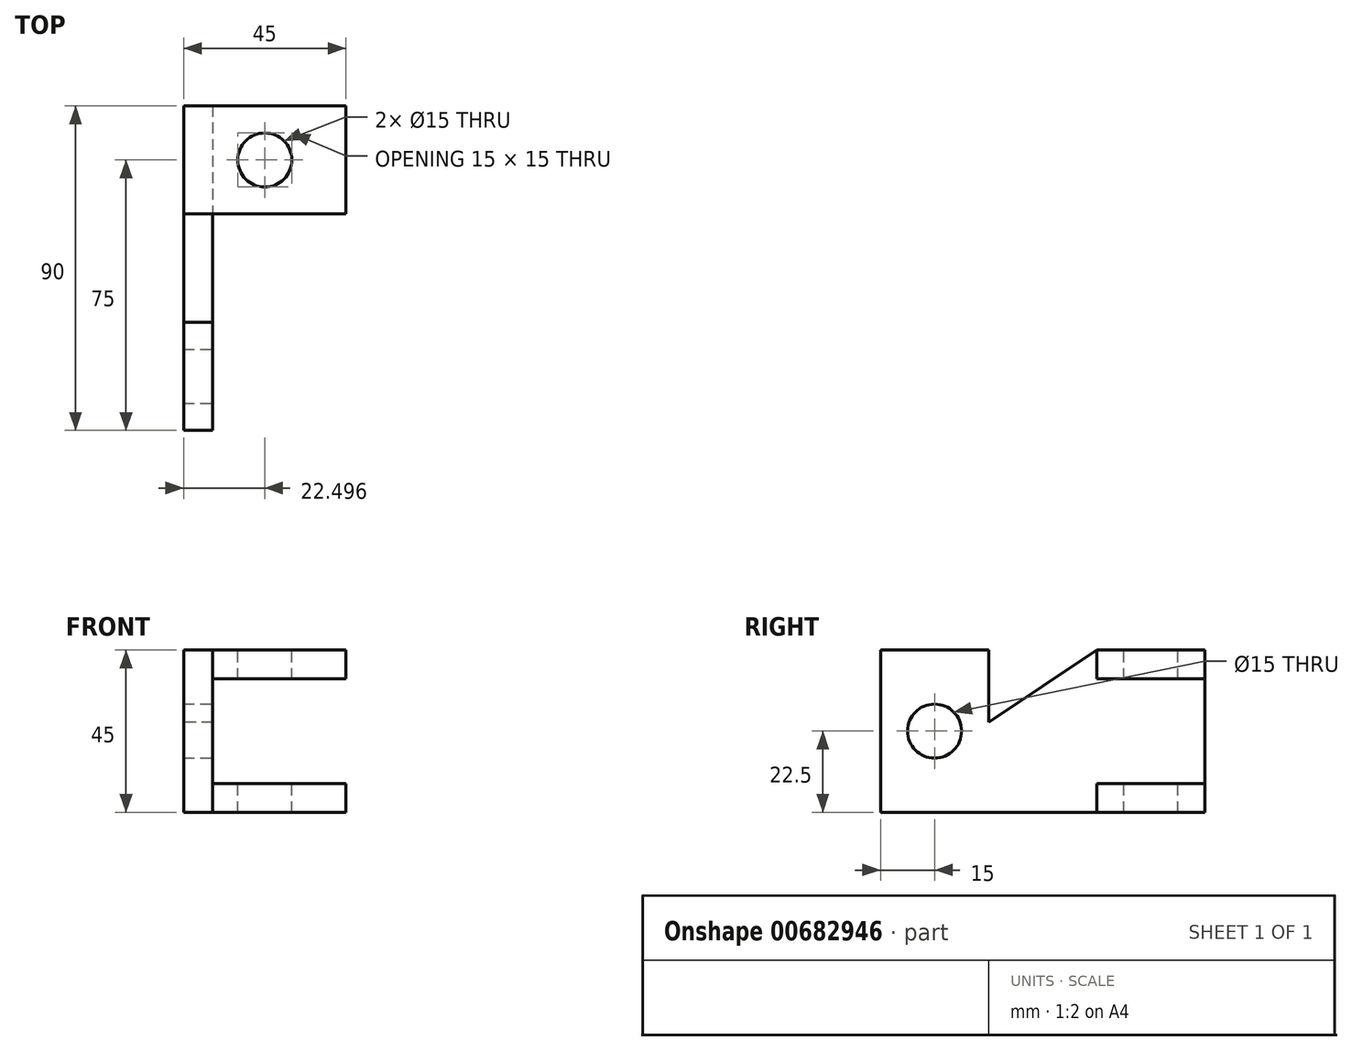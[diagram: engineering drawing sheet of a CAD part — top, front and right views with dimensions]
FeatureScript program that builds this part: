
annotation { "Feature Type Name" : "Feature", "Feature Type Description" : "" }
export const myFeature = defineFeature(function(context is Context, id is Id, definition is map)
    precondition{}
    {
        {
            var Q0;
            Q0=qCreatedBy(makeId("Right.planeOp"),FACE);
            var sketch = newSketch(context, id + "F0", { "sketchPlane" : qUnion([Q0])});
            skLineSegment(sketch, "E0", {"start": v(0, 45) * mm, "end": v(0, 0) * mm});
            skLineSegment(sketch, "E1", {"start": v(0, 0) * mm, "end": v(90, 0) * mm});
            skLineSegment(sketch, "E2", {"start": v(90, 0) * mm, "end": v(90, 45) * mm});
            skLineSegment(sketch, "E3", {"start": v(90, 45) * mm, "end": v(60, 45) * mm});
            skLineSegment(sketch, "E4", {"start": v(60, 45) * mm, "end": v(30, 25) * mm});
            skLineSegment(sketch, "E5", {"start": v(30, 25) * mm, "end": v(30, 45) * mm});
            skLineSegment(sketch, "E6", {"start": v(30, 45) * mm, "end": v(0, 45) * mm});
            skSolve(sketch);
        }
        {
            var Q0;
            Q0 = qSketchRegion(id + "F0", true);
            extrude(context, id + "F1", {"entities" : qUnion([Q0]), "depth" : 8 * mm, "offsetDistance" : 25.4 * mm});
        }
        {
            var Q0;
            Q0=makeQuery(id+"F1.opExtrude","CAP_FACE",FACE,{"disambiguationData":[OSD([sQuery(id+"F0.wireOp",EDGE,"E0"),sQuery(id+"F0.wireOp",EDGE,"E1"),sQuery(id+"F0.wireOp",EDGE,"E2"),sQuery(id+"F0.wireOp",EDGE,"E3"),sQuery(id+"F0.wireOp",EDGE,"E4"),sQuery(id+"F0.wireOp",EDGE,"E5"),sQuery(id+"F0.wireOp",EDGE,"E6")])],"isStart":false});
            var sketch = newSketch(context, id + "F2", { "sketchPlane" : qUnion([Q0])});
            skLineSegment(sketch, "E7.bottom", {"start": v(90, 45) * mm, "end": v(60, 45) * mm});
            skLineSegment(sketch, "E7.top", {"start": v(90, 37) * mm, "end": v(60, 37) * mm});
            skLineSegment(sketch, "E7.left", {"start": v(90, 45) * mm, "end": v(90, 37) * mm});
            skLineSegment(sketch, "E7.right", {"start": v(60, 45) * mm, "end": v(60, 37) * mm});
            skLineSegment(sketch, "E8.bottom", {"start": v(90, 0) * mm, "end": v(60, 0) * mm});
            skLineSegment(sketch, "E8.top", {"start": v(90, 8) * mm, "end": v(60, 8) * mm});
            skLineSegment(sketch, "E8.left", {"start": v(90, 0) * mm, "end": v(90, 8) * mm});
            skLineSegment(sketch, "E8.right", {"start": v(60, 0) * mm, "end": v(60, 8) * mm});
            skLineSegment(sketch, "E9", {"start": v(15, 45) * mm, "end": v(15, 22.5) * mm});
            skSolve(sketch);
        }
        {
            var Q0;
            Q0 = qSketchRegion(id + "F2", true);
            extrude(context, id + "F3", {"entities" : qUnion([Q0]), "operationType" : NewBodyOperationType.ADD, "depth" : 37 * mm, "offsetDistance" : 25.4 * mm});
        }
        {
            var Q0;
            Q0=makeQuery(id+"F3.boolean.opBoolean","MERGE",FACE,{"derivedFrom":[makeQuery(id+"F1.opExtrude","SWEPT_FACE",FACE,{"disambiguationData":[OSD([sQuery(id+"F0.wireOp",EDGE,"E3")])]}),makeQuery(id+"F3.opExtrude","SWEPT_FACE",FACE,{"disambiguationData":[OSD([sQuery(id+"F2.wireOp",EDGE,"E7.bottom")])]})]});
            var sketch = newSketch(context, id + "F4", { "sketchPlane" : qUnion([Q0])});
            skCircle(sketch, "E10", {"center": v(22.5, 75) * mm, "radius": 7.5 * mm});
            skSolve(sketch);
        }
        {
            var Q0;
            Q0=sQuery(id+"F4.wireOp",VERTEX,"E10.center");
            var Q1;
            Q1=makeQuery(id+"F1.opExtrude","SWEPT_BODY",BODY,{"disambiguationData":[OSD([sQuery(id+"F0.wireOp",EDGE,"E0"),sQuery(id+"F0.wireOp",EDGE,"E1"),sQuery(id+"F0.wireOp",EDGE,"E2"),sQuery(id+"F0.wireOp",EDGE,"E3"),sQuery(id+"F0.wireOp",EDGE,"E4"),sQuery(id+"F0.wireOp",EDGE,"E5"),sQuery(id+"F0.wireOp",EDGE,"E6")])]});
            hole(context, id + "F5", {"style" : HoleStyle.SIMPLE, "endStyle" : HoleEndStyle.THROUGH, "holeDiameter" : 15 * mm, "majorDiameter" : 6.35 * mm, "isTappedThrough" : true, "tappedDepth" : 12.7 * mm, "tapClearance" : 3, "locations" : qUnion([Q0]), "scope" : qUnion([Q1])});
        }
        {
            var Q0;
            Q0=sQuery(id+"F2.wireOp",VERTEX,"E9.end");
            var Q1;
            Q1=makeQuery(id+"F1.opExtrude","SWEPT_BODY",BODY,{"disambiguationData":[OSD([sQuery(id+"F0.wireOp",EDGE,"E0"),sQuery(id+"F0.wireOp",EDGE,"E1"),sQuery(id+"F0.wireOp",EDGE,"E2"),sQuery(id+"F0.wireOp",EDGE,"E3"),sQuery(id+"F0.wireOp",EDGE,"E4"),sQuery(id+"F0.wireOp",EDGE,"E5"),sQuery(id+"F0.wireOp",EDGE,"E6")])]});
            hole(context, id + "F6", {"style" : HoleStyle.SIMPLE, "endStyle" : HoleEndStyle.THROUGH, "holeDiameter" : 15 * mm, "majorDiameter" : 6.35 * mm, "isTappedThrough" : true, "tappedDepth" : 12.7 * mm, "tapClearance" : 3, "locations" : qUnion([Q0]), "scope" : qUnion([Q1])});
        }
    });
